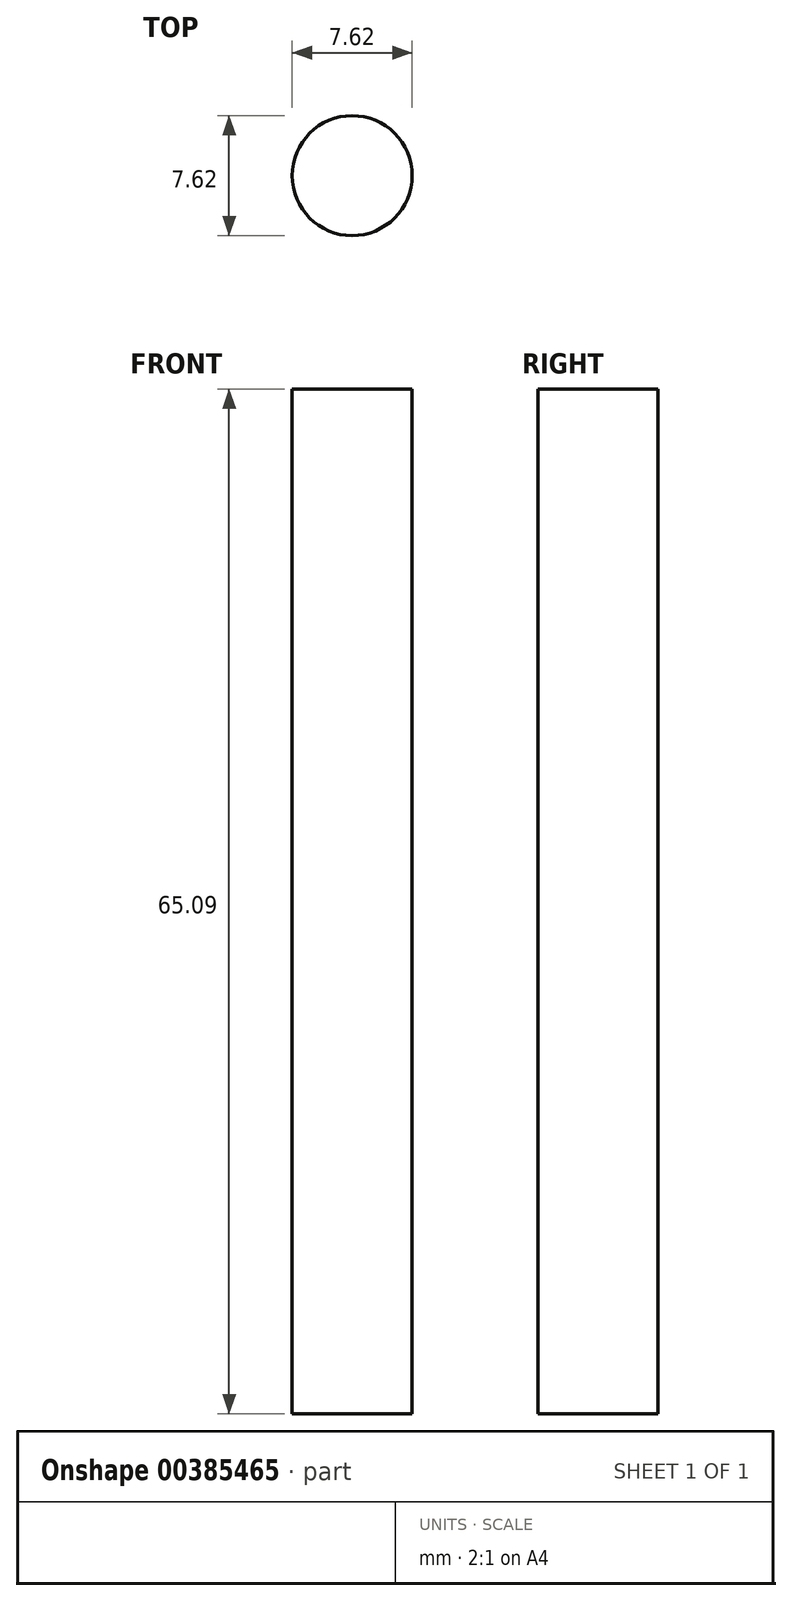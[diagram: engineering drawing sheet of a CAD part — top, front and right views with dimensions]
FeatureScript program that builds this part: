
annotation { "Feature Type Name" : "Feature", "Feature Type Description" : "" }
export const myFeature = defineFeature(function(context is Context, id is Id, definition is map)
    precondition{}
    {
        {
            var Q0;
            Q0=qCreatedBy(makeId("Top.planeOp"),FACE);
            var sketch = newSketch(context, id + "F0", { "sketchPlane" : qUnion([Q0])});
            skCircle(sketch, "E0", {"center": v(0, 0) * mm, "radius": 3.81 * mm});
            skSolve(sketch);
        }
        {
            var Q0;
            Q0 = qSketchRegion(id + "F0", true);
            extrude(context, id + "F1", {"entities" : qUnion([Q0]), "depth" : 65.1 * mm});
        }
    });
